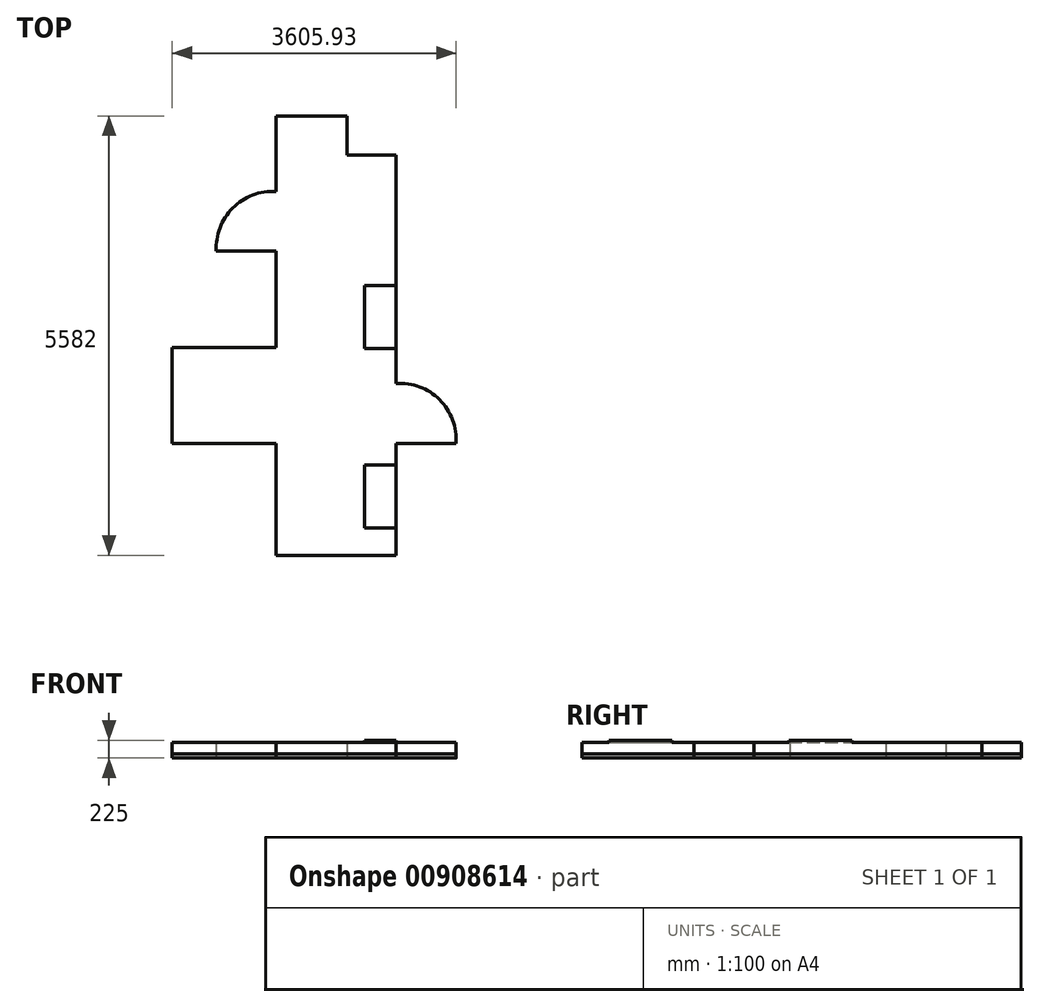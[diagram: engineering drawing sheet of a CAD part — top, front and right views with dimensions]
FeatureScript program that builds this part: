
annotation { "Feature Type Name" : "Feature", "Feature Type Description" : "" }
export const myFeature = defineFeature(function(context is Context, id is Id, definition is map)
    precondition{}
    {
        {
            var Q0;
            Q0=qCreatedBy(makeId("Top.planeOp"),FACE);
            var sketch = newSketch(context, id + "F0", { "sketchPlane" : qUnion([Q0])});
            skLineSegment(sketch, "E0.top", {"start": v(-1124, -913.71) * mm, "end": v(400, -913.71) * mm});
            skLineSegment(sketch, "E0.right", {"start": v(400, 4168.29) * mm, "end": v(400, -913.71) * mm});
            skLineSegment(sketch, "E1", {"start": v(-1124, -913.71) * mm, "end": v(-1124, 508.29) * mm, "construction": true});
            skLineSegment(sketch, "E2", {"start": v(-1124, 508.29) * mm, "end": v(-2444, 508.29) * mm});
            skLineSegment(sketch, "E3", {"start": v(-1124, 1728.29) * mm, "end": v(-2444, 1728.29) * mm});
            skLineSegment(sketch, "E4", {"start": v(-2444, 1728.29) * mm, "end": v(-2444, 508.29) * mm});
            skLineSegment(sketch, "E5", {"start": v(-1124, 1728.29) * mm, "end": v(-1124, 2948.29) * mm, "construction": true});
            skLineSegment(sketch, "E6", {"start": v(-1124, 2948.29) * mm, "end": v(-1884, 2948.29) * mm});
            skLineSegment(sketch, "E7", {"start": v(-1124, 2948.29) * mm, "end": v(-1124, 3708.29) * mm});
            skArc(sketch, "E8", {"start": v(-1124, 3708.29) * mm, "mid": v(-1673.93, 3498.22) * mm, "end": v(-1884, 2948.29) * mm});
            skLineSegment(sketch, "E9", {"start": v(400, 508.29) * mm, "end": v(1160, 508.29) * mm});
            skLineSegment(sketch, "E10", {"start": v(400, 508.29) * mm, "end": v(400, 1268.29) * mm});
            skArc(sketch, "E11", {"start": v(1160, 508.29) * mm, "mid": v(954.08, 1062.37) * mm, "end": v(400, 1268.29) * mm});
            skLineSegment(sketch, "E12", {"start": v(-224, 4168.29) * mm, "end": v(-224, 4668.29) * mm});
            skLineSegment(sketch, "E13", {"start": v(-224, 4668.29) * mm, "end": v(-1124, 4668.29) * mm});
            skLineSegment(sketch, "E14", {"start": v(-1124, 4168.29) * mm, "end": v(-1124, 4668.29) * mm});
            skLineSegment(sketch, "E15", {"start": v(-1124, -913.71) * mm, "end": v(-1124, 508.29) * mm});
            skLineSegment(sketch, "E16", {"start": v(-1124, 1728.29) * mm, "end": v(-1124, 2948.29) * mm});
            skLineSegment(sketch, "E17", {"start": v(-1124, 3708.29) * mm, "end": v(-1124, 4168.29) * mm});
            skLineSegment(sketch, "E18", {"start": v(-224, 4168.29) * mm, "end": v(400, 4168.29) * mm});
            skLineSegment(sketch, "E19.left", {"start": v(400, 1627.29) * mm, "end": v(400, 2427.29) * mm});
            skLineSegment(sketch, "E20.left", {"start": v(400, 330.12) * mm, "end": v(400, -477.1) * mm});
            skSolve(sketch);
        }
        {
            var Q0;
            Q0=makeQuery(id+"F0.imprint","IMPRINT",FACE,{"disambiguationData":[TD([[makeQuery(id+"F0.imprint","IMPRINT",EDGE,{"derivedFrom":sQuery(id+"F0.wireOp",EDGE,"E6")}),-1.0]])]});
            var Q1;
            {var subQ0=sQuery(id+"F0.wireOp",EDGE,"E2");Q1=makeQuery(id+"F0.imprint","IMPRINT",FACE,{"disambiguationData":[TD([[makeQuery(id+"F0.imprint","IMPRINT",EDGE,{"derivedFrom":subQ0}),-1.0]])]});}
            var Q2;
            Q2=makeQuery(id+"F0.imprint","IMPRINT",FACE,{"disambiguationData":[TD([[makeQuery(id+"F0.imprint","IMPRINT",EDGE,{"derivedFrom":sQuery(id+"F0.wireOp",EDGE,"E9")}),1.0]])]});
            var Q3;
            Q3=makeQuery(id+"F0.imprint","IMPRINT",FACE,{"disambiguationData":[TD([[makeQuery(id+"F0.imprint","IMPRINT",EDGE,{"derivedFrom":sQuery(id+"F0.wireOp",EDGE,"w0C0WAWq-DIYK-ycJx-IpEQ-NjDQX30WZSY3")}),1.0]])]});
            extrude(context, id + "F1", {"entities" : qUnion([Q0, Q1, Q2, Q3]), "depth" : 200 * mm, "offsetDistance" : 25 * mm});
        }
        {
            var Q0;
            Q0 = qSketchRegion(id + "F0", true);
            extrude(context, id + "F2", {"entities" : qUnion([Q0]), "depth" : 50 * mm, "offsetDistance" : 25 * mm});
        }
        {
            var Q0;
            Q0=makeQuery(id+"F1.opExtrude","CAP_FACE",FACE,{"disambiguationData":[OSD([sQuery(id+"F0.wireOp",EDGE,"E0.top"),sQuery(id+"F0.wireOp",EDGE,"E0.right"),sQuery(id+"F0.wireOp",EDGE,"E2"),sQuery(id+"F0.wireOp",EDGE,"E3"),sQuery(id+"F0.wireOp",EDGE,"E4"),sQuery(id+"F0.wireOp",EDGE,"E6"),sQuery(id+"F0.wireOp",EDGE,"E8"),sQuery(id+"F0.wireOp",EDGE,"E9"),sQuery(id+"F0.wireOp",EDGE,"E11"),sQuery(id+"F0.wireOp",EDGE,"E12"),sQuery(id+"F0.wireOp",EDGE,"E13"),sQuery(id+"F0.wireOp",EDGE,"E14"),sQuery(id+"F0.wireOp",EDGE,"E15"),sQuery(id+"F0.wireOp",EDGE,"E16"),sQuery(id+"F0.wireOp",EDGE,"E17"),sQuery(id+"F0.wireOp",EDGE,"E18"),sQuery(id+"F0.wireOp",EDGE,"E19.left"),sQuery(id+"F0.wireOp",EDGE,"E20.left")])],"isStart":false});
            var sketch = newSketch(context, id + "F3", { "sketchPlane" : qUnion([Q0])});
            skLineSegment(sketch, "E21.bottom", {"start": v(400, 1714.2) * mm, "end": v(0, 1714.2) * mm});
            skLineSegment(sketch, "E21.top", {"start": v(400, 2514.2) * mm, "end": v(0, 2514.2) * mm});
            skLineSegment(sketch, "E21.left", {"start": v(400, 1714.2) * mm, "end": v(400, 2514.2) * mm});
            skLineSegment(sketch, "E21.right", {"start": v(0, 1714.2) * mm, "end": v(0, 2514.2) * mm});
            skLineSegment(sketch, "E22.bottom", {"start": v(400, -568.29) * mm, "end": v(0, -568.29) * mm});
            skLineSegment(sketch, "E22.top", {"start": v(400, 231.71) * mm, "end": v(0, 231.71) * mm});
            skLineSegment(sketch, "E22.left", {"start": v(400, -568.29) * mm, "end": v(400, 231.71) * mm});
            skLineSegment(sketch, "E22.right", {"start": v(0, -568.29) * mm, "end": v(0, 231.71) * mm});
            skSolve(sketch);
        }
        {
            var Q0;
            Q0 = qSketchRegion(id + "F3", true);
            extrude(context, id + "F4", {"entities" : qUnion([Q0]), "operationType" : NewBodyOperationType.ADD, "depth" : 25 * mm, "offsetDistance" : 25 * mm});
        }
    });
